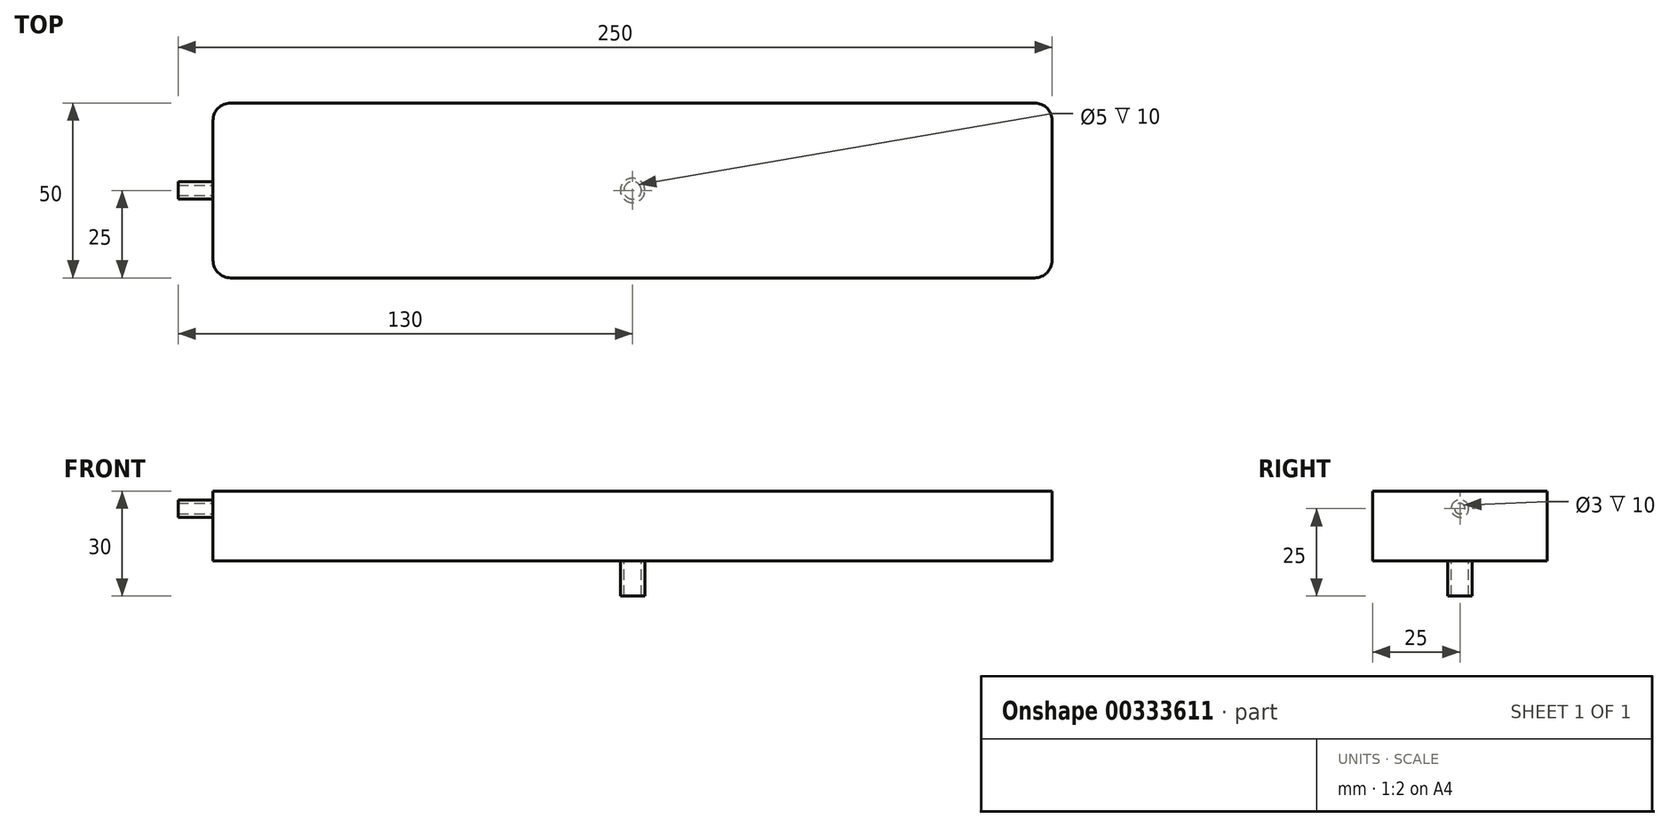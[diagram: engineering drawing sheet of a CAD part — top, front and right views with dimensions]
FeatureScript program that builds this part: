
annotation { "Feature Type Name" : "Feature", "Feature Type Description" : "" }
export const myFeature = defineFeature(function(context is Context, id is Id, definition is map)
    precondition{}
    {
        {
            var Q0;
            Q0=qCreatedBy(makeId("Top.planeOp"),FACE);
            var sketch = newSketch(context, id + "F0", { "sketchPlane" : qUnion([Q0])});
            skLineSegment(sketch, "E0.bottom", {"start": v(-120, 25) * mm, "end": v(120, 25) * mm});
            skLineSegment(sketch, "E0.top", {"start": v(-120, -25) * mm, "end": v(120, -25) * mm});
            skLineSegment(sketch, "E0.left", {"start": v(-120, 25) * mm, "end": v(-120, -25) * mm});
            skLineSegment(sketch, "E0.right", {"start": v(120, 25) * mm, "end": v(120, -25) * mm});
            skCircle(sketch, "E1", {"center": v(0, 0) * mm, "radius": 3.5 * mm});
            skPoint(sketch, "E1.centerSnap0", {"position": v(-120, 0) * mm});
            skSolve(sketch);
        }
        {
            var Q0;
            Q0=makeQuery(id+"F0.imprint","IMPRINT",FACE,{"disambiguationData":[TD([[makeQuery(id+"F0.imprint","IMPRINT",EDGE,{"derivedFrom":sQuery(id+"F0.wireOp",EDGE,"E0.bottom")}),-1.0]])]});
            var Q1;
            Q1=makeQuery(id+"F0.imprint","IMPRINT",FACE,{"disambiguationData":[TD([[makeQuery(id+"F0.imprint","IMPRINT",EDGE,{"derivedFrom":sQuery(id+"F0.wireOp",EDGE,"E1")}),1.0]])]});
            extrude(context, id + "F1", {"entities" : qUnion([Q0, Q1]), "depth" : 20 * mm});
        }
        {
            var Q0;
            Q0=makeQuery(id+"F1.opExtrude","SWEPT_EDGE",EDGE,{"disambiguationData":[OSD([sQuery(id+"F0.wireOp",EDGE,"E0.top"),sQuery(id+"F0.wireOp",EDGE,"E0.left")])]});
            var Q1;
            Q1=makeQuery(id+"F1.opExtrude","SWEPT_EDGE",EDGE,{"disambiguationData":[OSD([sQuery(id+"F0.wireOp",EDGE,"E0.top"),sQuery(id+"F0.wireOp",EDGE,"E0.right")])]});
            var Q2;
            Q2=makeQuery(id+"F1.opExtrude","SWEPT_EDGE",EDGE,{"disambiguationData":[OSD([sQuery(id+"F0.wireOp",EDGE,"E0.bottom"),sQuery(id+"F0.wireOp",EDGE,"E0.right")])]});
            var Q3;
            Q3=makeQuery(id+"F1.opExtrude","SWEPT_EDGE",EDGE,{"disambiguationData":[OSD([sQuery(id+"F0.wireOp",EDGE,"E0.bottom"),sQuery(id+"F0.wireOp",EDGE,"E0.left")])]});
            fillet(context, id + "F2", {"entities" : qUnion([Q0, Q1, Q2, Q3]), "radius" : 5 * mm, "tangentPropagation" : true, "allowEdgeOverflow" : false});
        }
        {
            var Q0;
            {var subQ0=sQuery(id+"F0.wireOp",EDGE,"E0.left");var subQ1=makeQuery(id+"F1.opExtrude","SWEPT_FACE",FACE,{"disambiguationData":[OSD([subQ0])]});var subQ2=sQuery(id+"F0.wireOp",EDGE,"E0.bottom");Q0=makeQuery(id+"F4frkugCjGHrMax_1.boolean.opBoolean","MERGE",FACE,{"derivedFrom":[makeQuery(id+"Fw4IjNx5JeH9Sb3_1.opShell","OFFSET_FACE",FACE,{"disambiguationData":[OSD([subQ0])]}),subQ1,makeQuery(id+"F4frkugCjGHrMax_1.opExtrude","SWEPT_FACE",FACE,{"disambiguationData":[OSD([subQ2,subQ0]),TDD([makeQuery(id+"Fw4IjNx5JeH9Sb3_1.opShell","OFFSET_EDGE",EDGE,{"disambiguationData":[OSD([subQ2,subQ0]),TDD([makeQuery(id+"F2.opFillet","BLEND_EDGE",EDGE,{"blendedFrom":[makeQuery(id+"F1.opExtrude","SWEPT_EDGE",EDGE,{"disambiguationData":[OSD([subQ2,subQ0])]}),subQ1],"blendedInto":[subQ1]})]),OD(1.0)]})])]})]});}
            var sketch = newSketch(context, id + "F3", { "sketchPlane" : qUnion([Q0])});
            skCircle(sketch, "E2", {"center": v(0, 15) * mm, "radius": 2.5 * mm});
            skPoint(sketch, "E2.centerSnap0", {"position": v(0, 20) * mm});
            skCircle(sketch, "E3", {"center": v(0, 15) * mm, "radius": 1.5 * mm});
            skSolve(sketch);
        }
        {
            var Q0;
            Q0=makeQuery(id+"F1.opExtrude","CAP_FACE",FACE,{"disambiguationData":[OSD([sQuery(id+"F0.wireOp",EDGE,"E0.bottom"),sQuery(id+"F0.wireOp",EDGE,"E0.top"),sQuery(id+"F0.wireOp",EDGE,"E0.left"),sQuery(id+"F0.wireOp",EDGE,"E0.right")])],"isStart":true});
            var sketch = newSketch(context, id + "F4", { "sketchPlane" : qUnion([Q0])});
            skCircle(sketch, "E4", {"center": v(0, 0) * mm, "radius": 3.5 * mm});
            skCircle(sketch, "E5", {"center": v(0, 0) * mm, "radius": 2.5 * mm});
            skSolve(sketch);
        }
        {
            var Q0;
            Q0=makeQuery(id+"F4.imprint","IMPRINT",FACE,{"disambiguationData":[TD([[makeQuery(id+"F4.imprint","IMPRINT",EDGE,{"derivedFrom":sQuery(id+"F4.wireOp",EDGE,"E4")}),1.0]])]});
            extrude(context, id + "F5", {"entities" : qUnion([Q0]), "operationType" : NewBodyOperationType.ADD, "depth" : 10 * mm});
        }
        {
            var Q0;
            Q0=makeQuery(id+"F3.imprint","IMPRINT",FACE,{"disambiguationData":[TD([[makeQuery(id+"F3.imprint","IMPRINT",EDGE,{"derivedFrom":sQuery(id+"F3.wireOp",EDGE,"E2")}),1.0]])]});
            extrude(context, id + "F6", {"entities" : qUnion([Q0]), "operationType" : NewBodyOperationType.ADD, "depth" : 10 * mm});
        }
    });
